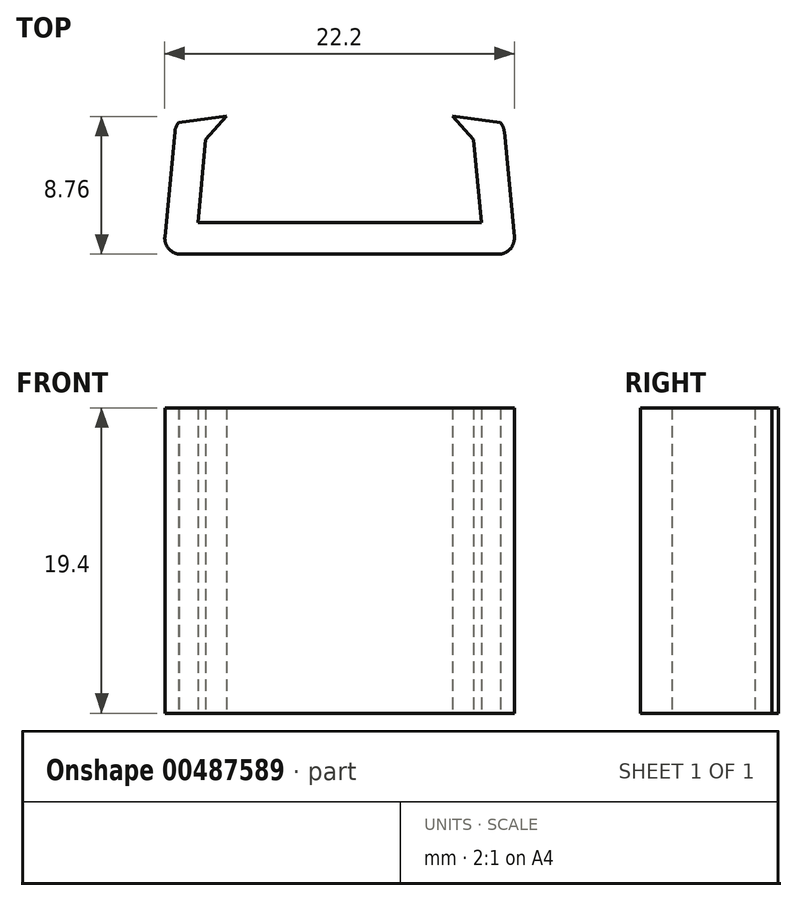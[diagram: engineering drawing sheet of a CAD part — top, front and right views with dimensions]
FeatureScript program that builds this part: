
annotation { "Feature Type Name" : "Feature", "Feature Type Description" : "" }
export const myFeature = defineFeature(function(context is Context, id is Id, definition is map)
    precondition{}
    {
        {
            var Q0;
            Q0=qCreatedBy(makeId("Top.planeOp"),FACE);
            var sketch = newSketch(context, id + "F0", { "sketchPlane" : qUnion([Q0])});
            skLineSegment(sketch, "E0", {"start": v(0, 0) * mm, "end": v(-9, 0) * mm});
            skLineSegment(sketch, "E1", {"start": v(0, 5.28) * mm, "end": v(-8.5, 5.28) * mm, "construction": true});
            skLineSegment(sketch, "E2", {"start": v(-9, 0) * mm, "end": v(-8.5, 5.28) * mm});
            skLineSegment(sketch, "E3", {"start": v(-8.5, 5.28) * mm, "end": v(-7.16, 6.76) * mm});
            skLineSegment(sketch, "E4", {"start": v(-10.46, 5.8) * mm, "end": v(-11.1, -0.9) * mm});
            skLineSegment(sketch, "E5", {"start": v(-10.1, -2) * mm, "end": v(0, -2) * mm});
            skLineSegment(sketch, "E6", {"start": v(-10.22, 6.35) * mm, "end": v(-10.2, 6.37) * mm});
            skPoint(sketch, "E7.visualSharp", {"position": v(-11.2, -2) * mm});
            skArc(sketch, "E7.filletArc", {"start": v(-11.1, -0.9) * mm, "mid": v(-10.84, -1.67) * mm, "end": v(-10.1, -2) * mm});
            skPoint(sketch, "E8.visualSharp", {"position": v(-10.43, 6.12) * mm});
            skArc(sketch, "E8.filletArc", {"start": v(-10.2, 6.37) * mm, "mid": v(-10.38, 6.1) * mm, "end": v(-10.46, 5.8) * mm});
            skLineSegment(sketch, "E9", {"start": v(-10.22, 6.35) * mm, "end": v(-7.16, 6.76) * mm});
            skLineSegment(sketch, "E10.MirrorCS", {"start": v(10.22, 6.35) * mm, "end": v(10.2, 6.37) * mm});
            skLineSegment(sketch, "E11.MirrorCS", {"start": v(0, 5.28) * mm, "end": v(8.5, 5.28) * mm, "construction": true});
            skLineSegment(sketch, "E12.MirrorCS", {"start": v(8.5, 5.28) * mm, "end": v(7.16, 6.76) * mm});
            skArc(sketch, "E13.MirrorCS", {"start": v(10.2, 6.37) * mm, "mid": v(10.38, 6.1) * mm, "end": v(10.46, 5.8) * mm});
            skLineSegment(sketch, "E14.MirrorCS", {"start": v(9, 0) * mm, "end": v(8.5, 5.28) * mm});
            skLineSegment(sketch, "E15.MirrorCS", {"start": v(10.46, 5.8) * mm, "end": v(11.1, -0.9) * mm});
            skLineSegment(sketch, "E16.MirrorCS", {"start": v(10.22, 6.35) * mm, "end": v(7.16, 6.76) * mm});
            skLineSegment(sketch, "E17.MirrorCS", {"start": v(10.1, -2) * mm, "end": v(0, -2) * mm});
            skLineSegment(sketch, "E18.MirrorCS", {"start": v(0, 0) * mm, "end": v(9, 0) * mm});
            skPoint(sketch, "E19.MirrorP", {"position": v(11.2, -2) * mm});
            skArc(sketch, "E20.MirrorCS", {"start": v(11.1, -0.9) * mm, "mid": v(10.84, -1.67) * mm, "end": v(10.1, -2) * mm});
            skSolve(sketch);
        }
        {
            var Q0;
            Q0 = qSketchRegion(id + "F0", true);
            extrude(context, id + "F1", {"entities" : qUnion([Q0]), "depth" : 19.4 * mm});
        }
    });
